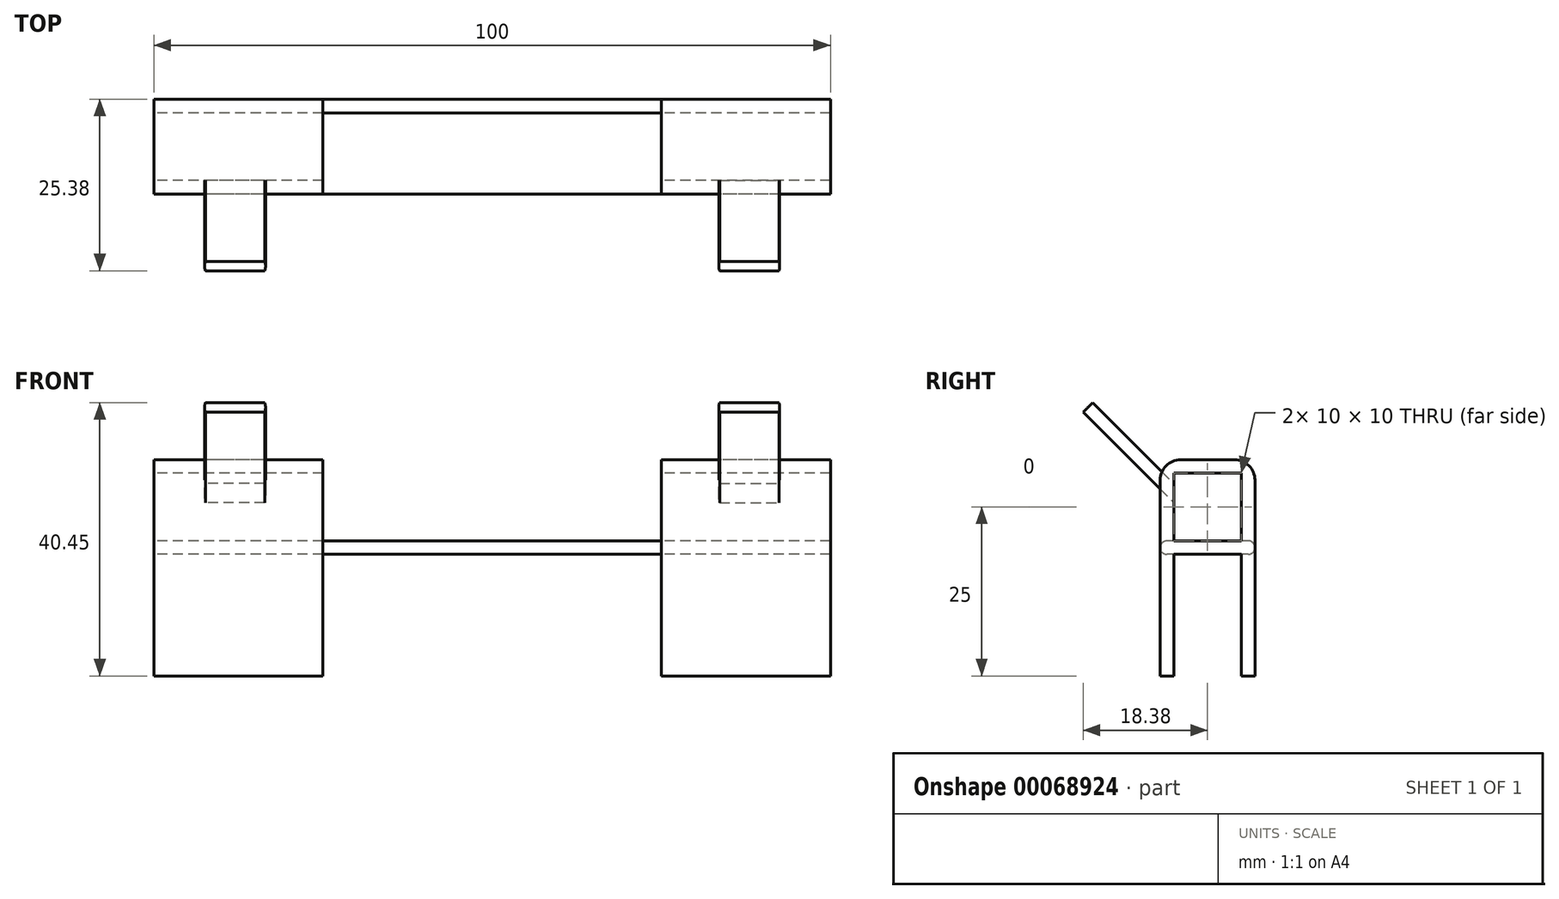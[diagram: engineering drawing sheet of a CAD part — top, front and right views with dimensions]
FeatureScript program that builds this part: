
annotation { "Feature Type Name" : "Feature", "Feature Type Description" : "" }
export const myFeature = defineFeature(function(context is Context, id is Id, definition is map)
    precondition{}
    {
        {
            var Q0;
            Q0=qCreatedBy(makeId("Front.planeOp"),FACE);
            var sketch = newSketch(context, id + "F0", { "sketchPlane" : qUnion([Q0])});
            skCircle(sketch, "E0", {"center": v(-38, 22.06) * mm, "radius": 7 * mm});
            skLineSegment(sketch, "E1", {"start": v(-38, 22.06) * mm, "end": v(-21.61, 22.06) * mm, "construction": true});
            skCircle(sketch, "E2", {"center": v(-38, 22.06) * mm, "radius": 4.5 * mm});
            skLineSegment(sketch, "E3.bottom", {"start": v(-50, 23.06) * mm, "end": v(0, 23.06) * mm});
            skLineSegment(sketch, "E3.top", {"start": v(-50, 21.06) * mm, "end": v(0, 21.06) * mm});
            skLineSegment(sketch, "E3.left", {"start": v(-50, 23.06) * mm, "end": v(-50, 21.06) * mm});
            skLineSegment(sketch, "E3.right", {"start": v(0, 23.06) * mm, "end": v(0, 21.06) * mm});
            skLineSegment(sketch, "E4", {"start": v(-50, 22.06) * mm, "end": v(0, 22.06) * mm, "construction": true});
            skLineSegment(sketch, "E5", {"start": v(0, 53.95) * mm, "end": v(0, 2.95) * mm, "construction": true});
            skLineSegment(sketch, "E6.MirrorCS", {"start": v(-50, 21.06) * mm, "end": v(-50, 23.06) * mm});
            skLineSegment(sketch, "E7.MirrorCS", {"start": v(0, 21.06) * mm, "end": v(0, 23.06) * mm});
            skCircle(sketch, "E8.MirrorC", {"center": v(38, 22.06) * mm, "radius": 7 * mm});
            skLineSegment(sketch, "E9.MirrorCS", {"start": v(50, 21.06) * mm, "end": v(50, 23.06) * mm});
            skCircle(sketch, "E10.MirrorC", {"center": v(38, 22.06) * mm, "radius": 4.5 * mm});
            skLineSegment(sketch, "E11.MirrorCS", {"start": v(50, 23.06) * mm, "end": v(50, 21.06) * mm});
            skLineSegment(sketch, "E12.MirrorCS", {"start": v(50, 23.06) * mm, "end": v(0, 23.06) * mm});
            skLineSegment(sketch, "E13.MirrorCS", {"start": v(50, 21.06) * mm, "end": v(0, 21.06) * mm});
            skLineSegment(sketch, "E14.MirrorCS", {"start": v(38, 22.06) * mm, "end": v(21.61, 22.06) * mm, "construction": true});
            skLineSegment(sketch, "E15.MirrorCS", {"start": v(50, 22.06) * mm, "end": v(0, 22.06) * mm, "construction": true});
            skSolve(sketch);
        }
        {
            var Q0;
            Q0=makeQuery(id+"F0.imprint","IMPRINT",FACE,{"disambiguationData":[TD([[makeQuery(id+"F0.imprint","IMPRINT",EDGE,{"derivedFrom":sQuery(id+"F0.wireOp",EDGE,"E2")}),1.0]])]});
            var Q1;
            Q1=makeQuery(id+"F0.imprint","IMPRINT",FACE,{"disambiguationData":[TD([[makeQuery(id+"F0.imprint","IMPRINT",EDGE,{"derivedFrom":sQuery(id+"F0.wireOp",EDGE,"E10.MirrorC")}),1.0]])]});
            var Q2;
            Q2=sQuery(id+"F0.wireOp",EDGE,"E0");
            extrude(context, id + "F1", {"entities" : qUnion([Q0, Q1]), "surfaceEntities" : qUnion([Q2]), "depth" : 25 * mm});
        }
        {
            var Q0;
            Q0=makeQuery(id+"F1.opExtrude","SWEPT_BODY",BODY,{"disambiguationData":[OSD([sQuery(id+"F0.wireOp",EDGE,"E2"),sQuery(id+"F0.wireOp",EDGE,"E0")])]});
            var Q1;
            Q1=makeQuery(id+"F1.opExtrude","SWEPT_BODY",BODY,{"disambiguationData":[OSD([sQuery(id+"F0.wireOp",EDGE,"E10.MirrorC"),sQuery(id+"F0.wireOp",EDGE,"E8.MirrorC")])]});
            var Q2;
            Q2=sQuery(id+"F0.wireOp",EDGE,"E4");
            var Q3;
            Q3=sQuery(id+"F0.wireOp",EDGE,"E15.MirrorCS");
            transform(context, id + "F2", {"entities" : qUnion([Q0, Q1]), "transformType" : TransformType.ROTATION, "transformAxis" : qUnion([Q3]), "angle" : 45 * degree, "makeCopy" : false});
        }
        {
            var Q0;
            Q0=qCreatedBy(makeId("Right.planeOp"),FACE);
            var sketch = newSketch(context, id + "F3", { "sketchPlane" : qUnion([Q0])});
            skLineSegment(sketch, "E16.bottom", {"start": v(5, 20) * mm, "end": v(-5, 20) * mm});
            skLineSegment(sketch, "E16.top", {"start": v(5, 30) * mm, "end": v(-5, 30) * mm});
            skLineSegment(sketch, "E16.left", {"start": v(5, 20) * mm, "end": v(5, 30) * mm});
            skLineSegment(sketch, "E16.right", {"start": v(-5, 20) * mm, "end": v(-5, 30) * mm});
            skLineSegment(sketch, "E17.bottom", {"start": v(7, 18) * mm, "end": v(-7, 18) * mm});
            skLineSegment(sketch, "E17.top", {"start": v(7, 32) * mm, "end": v(-7, 32) * mm});
            skLineSegment(sketch, "E17.left", {"start": v(7, 18) * mm, "end": v(7, 32) * mm});
            skLineSegment(sketch, "E17.right", {"start": v(-7, 18) * mm, "end": v(-7, 34) * mm});
            skLineSegment(sketch, "E18", {"start": v(-7, 18) * mm, "end": v(-7, 0) * mm});
            skLineSegment(sketch, "E19", {"start": v(-7, 0) * mm, "end": v(-5, 0) * mm});
            skLineSegment(sketch, "E20", {"start": v(-5, 0) * mm, "end": v(-5, 18) * mm});
            skLineSegment(sketch, "E21.MirrorCS", {"start": v(5, 0) * mm, "end": v(5, 18) * mm});
            skLineSegment(sketch, "E22.MirrorCS", {"start": v(7, 0) * mm, "end": v(5, 0) * mm});
            skLineSegment(sketch, "E23.MirrorCS", {"start": v(7, 18) * mm, "end": v(7, 0) * mm});
            skLineSegment(sketch, "E24", {"start": v(-7, 18) * mm, "end": v(7, 18) * mm});
            skLineSegment(sketch, "E25", {"start": v(7, 20.03) * mm, "end": v(5, 20) * mm});
            skLineSegment(sketch, "E26", {"start": v(-5, 20) * mm, "end": v(-7, 20) * mm});
            skLineSegment(sketch, "E27", {"start": v(-7, 20) * mm, "end": v(-7, 18) * mm});
            skSolve(sketch);
        }
        {
            var Q0;
            Q0 = qSketchRegion(id + "F3", true);
            extrude(context, id + "F4", {"entities" : qUnion([Q0]), "depth" : 50 * mm, "hasSecondDirection" : true, "secondDirectionOppositeDirection" : true, "secondDirectionDepth" : 50 * mm});
        }
        {
            var Q0;
            Q0 = qSketchRegion(id + "F3", true);
            extrude(context, id + "F5", {"entities" : qUnion([Q0]), "operationType" : NewBodyOperationType.REMOVE, "oppositeDirection" : true, "depth" : 25 * mm, "hasSecondDirection" : true, "secondDirectionOppositeDirection" : false, "secondDirectionDepth" : 25 * mm});
        }
        {
            var Q0;
            Q0=makeQuery(id+"F3.imprint","IMPRINT",FACE,{"disambiguationData":[TD([[makeQuery(id+"F3.imprint","IMPRINT",EDGE,{"derivedFrom":sQuery(id+"F3.wireOp",EDGE,"E16.bottom")}),1.0]])]});
            extrude(context, id + "F6", {"entities" : qUnion([Q0]), "depth" : 25 * mm, "hasSecondDirection" : true, "secondDirectionOppositeDirection" : true, "secondDirectionDepth" : 25 * mm});
        }
        {
            var Q0;
            Q0=makeQuery(id+"F3.imprint","IMPRINT",FACE,{"disambiguationData":[TD([[makeQuery(id+"F3.imprint","IMPRINT",EDGE,{"derivedFrom":sQuery(id+"F3.wireOp",EDGE,"E16.bottom")}),-1.0]])]});
            var Q1;
            Q1=sQuery(id+"F3.wireOp",EDGE,"E16.top");
            var Q2;
            Q2=sQuery(id+"F3.wireOp",EDGE,"E16.right");
            var Q3;
            Q3=sQuery(id+"F3.wireOp",EDGE,"E16.left");
            var Q4;
            Q4=sQuery(id+"F3.wireOp",EDGE,"E16.bottom");
            extrude(context, id + "F7", {"entities" : qUnion([Q0]), "operationType" : NewBodyOperationType.REMOVE, "surfaceEntities" : qUnion([Q1, Q2, Q3, Q4]), "oppositeDirection" : true, "depth" : 50 * mm, "hasSecondDirection" : true, "secondDirectionOppositeDirection" : false, "secondDirectionDepth" : 50 * mm});
        }
        {
            var Q0;
            {var subQ0=sQuery(id+"F3.wireOp",EDGE,"E27");var subQ1=sQuery(id+"F3.wireOp",EDGE,"E24");var subQ2=sQuery(id+"F3.wireOp",EDGE,"E23.MirrorCS");var subQ3=sQuery(id+"F3.wireOp",EDGE,"E22.MirrorCS");var subQ4=sQuery(id+"F3.wireOp",EDGE,"E21.MirrorCS");var subQ5=sQuery(id+"F3.wireOp",EDGE,"E20");var subQ6=sQuery(id+"F3.wireOp",EDGE,"E19");var subQ7=sQuery(id+"F3.wireOp",EDGE,"E18");var subQ8=sQuery(id+"F3.wireOp",EDGE,"E17.right");var subQ9=sQuery(id+"F3.wireOp",EDGE,"E17.left");var subQ10=sQuery(id+"F3.wireOp",EDGE,"E17.top");var subQ11=sQuery(id+"F3.wireOp",EDGE,"E16.right");var subQ12=sQuery(id+"F3.wireOp",EDGE,"E16.left");var subQ13=sQuery(id+"F3.wireOp",EDGE,"E16.top");var subQ14=sQuery(id+"F3.wireOp",EDGE,"E16.bottom");Q0=makeQuery(id+"F5.boolean.opBoolean","SPLIT",EDGE,{"disambiguationData":[TD([makeQuery(id+"F4.opExtrude","CAP_FACE",FACE,{"disambiguationData":[OSD([subQ14,subQ13,subQ12,subQ11,subQ10,subQ9,subQ8,subQ7,subQ6,subQ5,subQ4,subQ3,subQ2,subQ1,subQ0])],"isStart":false})])],"derivedFrom":makeQuery(id+"F4.opExtrude","SWEPT_EDGE",EDGE,{"disambiguationData":[OSD([subQ10,subQ9])]})});}
            var Q1;
            {var subQ0=sQuery(id+"F3.wireOp",EDGE,"E27");var subQ1=sQuery(id+"F3.wireOp",EDGE,"E24");var subQ2=sQuery(id+"F3.wireOp",EDGE,"E23.MirrorCS");var subQ3=sQuery(id+"F3.wireOp",EDGE,"E22.MirrorCS");var subQ4=sQuery(id+"F3.wireOp",EDGE,"E21.MirrorCS");var subQ5=sQuery(id+"F3.wireOp",EDGE,"E20");var subQ6=sQuery(id+"F3.wireOp",EDGE,"E19");var subQ7=sQuery(id+"F3.wireOp",EDGE,"E18");var subQ8=sQuery(id+"F3.wireOp",EDGE,"E17.right");var subQ9=sQuery(id+"F3.wireOp",EDGE,"E17.left");var subQ10=sQuery(id+"F3.wireOp",EDGE,"E17.top");var subQ11=sQuery(id+"F3.wireOp",EDGE,"E16.right");var subQ12=sQuery(id+"F3.wireOp",EDGE,"E16.left");var subQ13=sQuery(id+"F3.wireOp",EDGE,"E16.top");var subQ14=sQuery(id+"F3.wireOp",EDGE,"E16.bottom");Q1=makeQuery(id+"F5.boolean.opBoolean","SPLIT",EDGE,{"disambiguationData":[TD([makeQuery(id+"F4.opExtrude","CAP_FACE",FACE,{"disambiguationData":[OSD([subQ14,subQ13,subQ12,subQ11,subQ10,subQ9,subQ8,subQ7,subQ6,subQ5,subQ4,subQ3,subQ2,subQ1,subQ0])],"isStart":true})])],"derivedFrom":makeQuery(id+"F4.opExtrude","SWEPT_EDGE",EDGE,{"disambiguationData":[OSD([subQ10,subQ9])]})});}
            var Q2;
            {var subQ0=sQuery(id+"F3.wireOp",EDGE,"E27");var subQ1=sQuery(id+"F3.wireOp",EDGE,"E24");var subQ2=sQuery(id+"F3.wireOp",EDGE,"E23.MirrorCS");var subQ3=sQuery(id+"F3.wireOp",EDGE,"E22.MirrorCS");var subQ4=sQuery(id+"F3.wireOp",EDGE,"E21.MirrorCS");var subQ5=sQuery(id+"F3.wireOp",EDGE,"E20");var subQ6=sQuery(id+"F3.wireOp",EDGE,"E19");var subQ7=sQuery(id+"F3.wireOp",EDGE,"E18");var subQ8=sQuery(id+"F3.wireOp",EDGE,"E17.right");var subQ9=sQuery(id+"F3.wireOp",EDGE,"E17.left");var subQ10=sQuery(id+"F3.wireOp",EDGE,"E17.top");var subQ11=sQuery(id+"F3.wireOp",EDGE,"E16.right");var subQ12=sQuery(id+"F3.wireOp",EDGE,"E16.left");var subQ13=sQuery(id+"F3.wireOp",EDGE,"E16.top");var subQ14=sQuery(id+"F3.wireOp",EDGE,"E16.bottom");Q2=makeQuery(id+"F5.boolean.opBoolean","SPLIT",EDGE,{"disambiguationData":[TD([makeQuery(id+"F4.opExtrude","CAP_FACE",FACE,{"disambiguationData":[OSD([subQ14,subQ13,subQ12,subQ11,subQ10,subQ9,subQ8,subQ7,subQ6,subQ5,subQ4,subQ3,subQ2,subQ1,subQ0])],"isStart":false})])],"derivedFrom":makeQuery(id+"F4.opExtrude","SWEPT_EDGE",EDGE,{"disambiguationData":[OSD([subQ10,subQ8])]})});}
            var Q3;
            {var subQ0=sQuery(id+"F3.wireOp",EDGE,"E27");var subQ1=sQuery(id+"F3.wireOp",EDGE,"E24");var subQ2=sQuery(id+"F3.wireOp",EDGE,"E23.MirrorCS");var subQ3=sQuery(id+"F3.wireOp",EDGE,"E22.MirrorCS");var subQ4=sQuery(id+"F3.wireOp",EDGE,"E21.MirrorCS");var subQ5=sQuery(id+"F3.wireOp",EDGE,"E20");var subQ6=sQuery(id+"F3.wireOp",EDGE,"E19");var subQ7=sQuery(id+"F3.wireOp",EDGE,"E18");var subQ8=sQuery(id+"F3.wireOp",EDGE,"E17.right");var subQ9=sQuery(id+"F3.wireOp",EDGE,"E17.left");var subQ10=sQuery(id+"F3.wireOp",EDGE,"E17.top");var subQ11=sQuery(id+"F3.wireOp",EDGE,"E16.right");var subQ12=sQuery(id+"F3.wireOp",EDGE,"E16.left");var subQ13=sQuery(id+"F3.wireOp",EDGE,"E16.top");var subQ14=sQuery(id+"F3.wireOp",EDGE,"E16.bottom");Q3=makeQuery(id+"F5.boolean.opBoolean","SPLIT",EDGE,{"disambiguationData":[TD([makeQuery(id+"F4.opExtrude","CAP_FACE",FACE,{"disambiguationData":[OSD([subQ14,subQ13,subQ12,subQ11,subQ10,subQ9,subQ8,subQ7,subQ6,subQ5,subQ4,subQ3,subQ2,subQ1,subQ0])],"isStart":true})])],"derivedFrom":makeQuery(id+"F4.opExtrude","SWEPT_EDGE",EDGE,{"disambiguationData":[OSD([subQ10,subQ8])]})});}
            fillet(context, id + "F8", {"entities" : qUnion([Q0, Q1, Q2, Q3]), "radius" : 3 * mm, "tangentPropagation" : true, "allowEdgeOverflow" : false});
        }
        {
            var Q0;
            Q0=makeQuery(id+"F6.opExtrude","SWEPT_EDGE",EDGE,{"disambiguationData":[OSD([sQuery(id+"F3.wireOp",EDGE,"E17.right"),sQuery(id+"F3.wireOp",EDGE,"E26"),sQuery(id+"F3.wireOp",EDGE,"E27")])]});
            var Q1;
            Q1=makeQuery(id+"F6.opExtrude","SWEPT_EDGE",EDGE,{"disambiguationData":[OSD([sQuery(id+"F3.wireOp",EDGE,"E18"),sQuery(id+"F3.wireOp",EDGE,"E24"),sQuery(id+"F3.wireOp",EDGE,"E27")])]});
            var Q2;
            Q2=makeQuery(id+"F6.opExtrude","SWEPT_EDGE",EDGE,{"disambiguationData":[OSD([sQuery(id+"F3.wireOp",EDGE,"E17.left"),sQuery(id+"F3.wireOp",EDGE,"E25")])]});
            var Q3;
            Q3=makeQuery(id+"F6.opExtrude","SWEPT_EDGE",EDGE,{"disambiguationData":[OSD([sQuery(id+"F3.wireOp",EDGE,"E17.left"),sQuery(id+"F3.wireOp",EDGE,"E23.MirrorCS"),sQuery(id+"F3.wireOp",EDGE,"E24")])]});
            fillet(context, id + "F9", {"entities" : qUnion([Q0, Q1, Q2, Q3]), "radius" : 1 * mm, "tangentPropagation" : true, "allowEdgeOverflow" : false});
        }
    });
